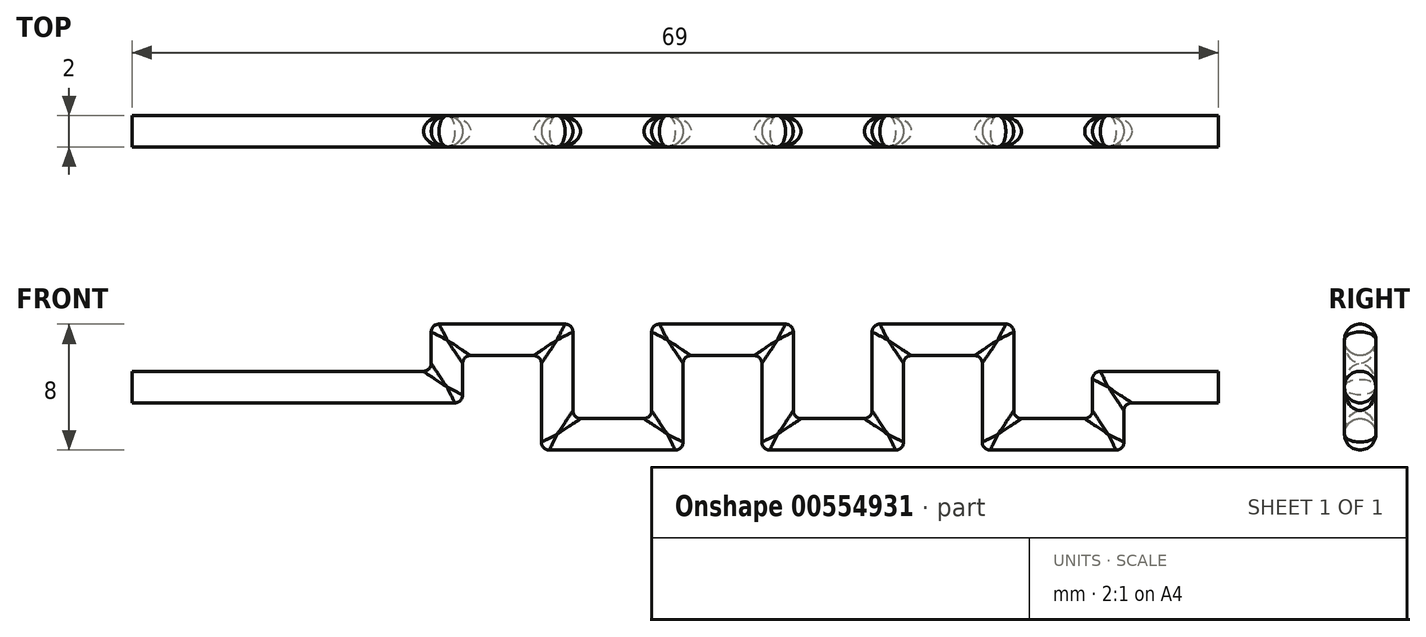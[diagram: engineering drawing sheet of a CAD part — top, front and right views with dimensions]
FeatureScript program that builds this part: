
annotation { "Feature Type Name" : "Feature", "Feature Type Description" : "" }
export const myFeature = defineFeature(function(context is Context, id is Id, definition is map)
    precondition{}
    {
        {
            var Q0;
            Q0=qCreatedBy(makeId("Front.planeOp"),FACE);
            var sketch = newSketch(context, id + "F0", { "sketchPlane" : qUnion([Q0])});
            skLineSegment(sketch, "E0", {"start": v(0, 0) * mm, "end": v(15, 0) * mm});
            skLineSegment(sketch, "E1", {"start": v(15, 0) * mm, "end": v(15, 3) * mm});
            skLineSegment(sketch, "E2", {"start": v(15, 3) * mm, "end": v(22, 3) * mm});
            skLineSegment(sketch, "E3", {"start": v(22, 3) * mm, "end": v(22, -3) * mm});
            skLineSegment(sketch, "E4", {"start": v(22, -3) * mm, "end": v(29, -3) * mm});
            skLineSegment(sketch, "E5", {"start": v(29, -3) * mm, "end": v(29, 3) * mm});
            skLineSegment(sketch, "E6", {"start": v(29, 3) * mm, "end": v(36, 3) * mm});
            skLineSegment(sketch, "E7", {"start": v(36, 3) * mm, "end": v(36, -3) * mm});
            skLineSegment(sketch, "E8", {"start": v(36, -3) * mm, "end": v(43, -3) * mm});
            skLineSegment(sketch, "E9", {"start": v(43, -3) * mm, "end": v(43, 3) * mm});
            skLineSegment(sketch, "E10", {"start": v(43, 3) * mm, "end": v(50, 3) * mm});
            skLineSegment(sketch, "E11", {"start": v(50, 3) * mm, "end": v(50, -3) * mm});
            skLineSegment(sketch, "E12", {"start": v(50, -3) * mm, "end": v(57, -3) * mm});
            skLineSegment(sketch, "E13", {"start": v(57, -3) * mm, "end": v(57, 0) * mm});
            skLineSegment(sketch, "E14.trimOffspring", {"start": v(57, 0) * mm, "end": v(64, 0) * mm});
            skSolve(sketch);
        }
        {
            var Q0;
            Q0=qCreatedBy(makeId("Right.planeOp"),FACE);
            var sketch = newSketch(context, id + "F1", { "sketchPlane" : qUnion([Q0])});
            skCircle(sketch, "E15", {"center": v(0, 0) * mm, "radius": 1 * mm});
            skSolve(sketch);
        }
        {
            var Q0;
            Q0=makeQuery(id+"F1.imprint","IMPRINT",FACE,{"disambiguationData":[TD([[makeQuery(id+"F1.imprint","IMPRINT",EDGE,{"derivedFrom":sQuery(id+"F1.wireOp",EDGE,"E15")}),1.0]])]});
            var Q1;
            Q1 = qConstructionFilter(qBodyType(qCreatedBy(id + "F0" ,EDGE), BodyType.WIRE), ConstructionObject.NO);
            sweep(context, id + "F2", {"profiles" : qUnion([Q0]), "path" : qUnion([Q1])});
        }
        {
            var Q0;
            Q0=makeQuery(id+"F2.opSweep","MID_CAP_EDGE",EDGE,{"disambiguationData":[OSD([sQuery(id+"F0.wireOp",VERTEX,"E14.trimOffspring.start"),sQuery(id+"F1.wireOp",EDGE,"E15")])],"capPos":14.0});
            var Q1;
            Q1=makeQuery(id+"F2.opSweep","MID_CAP_EDGE",EDGE,{"disambiguationData":[OSD([sQuery(id+"F0.wireOp",VERTEX,"E13.start"),sQuery(id+"F1.wireOp",EDGE,"E15")])],"capPos":13.0});
            var Q2;
            Q2=makeQuery(id+"F2.opSweep","MID_CAP_EDGE",EDGE,{"disambiguationData":[OSD([sQuery(id+"F0.wireOp",VERTEX,"E12.start"),sQuery(id+"F1.wireOp",EDGE,"E15")])],"capPos":12.0});
            var Q3;
            Q3=makeQuery(id+"F2.opSweep","MID_CAP_EDGE",EDGE,{"disambiguationData":[OSD([sQuery(id+"F0.wireOp",VERTEX,"E11.start"),sQuery(id+"F1.wireOp",EDGE,"E15")])],"capPos":11.0});
            var Q4;
            Q4=makeQuery(id+"F2.opSweep","MID_CAP_EDGE",EDGE,{"disambiguationData":[OSD([sQuery(id+"F0.wireOp",VERTEX,"E10.start"),sQuery(id+"F1.wireOp",EDGE,"E15")])],"capPos":10.0});
            var Q5;
            Q5=makeQuery(id+"F2.opSweep","MID_CAP_EDGE",EDGE,{"disambiguationData":[OSD([sQuery(id+"F0.wireOp",VERTEX,"E9.start"),sQuery(id+"F1.wireOp",EDGE,"E15")])],"capPos":9.0});
            var Q6;
            Q6=makeQuery(id+"F2.opSweep","MID_CAP_EDGE",EDGE,{"disambiguationData":[OSD([sQuery(id+"F0.wireOp",VERTEX,"E8.start"),sQuery(id+"F1.wireOp",EDGE,"E15")])],"capPos":8.0});
            var Q7;
            Q7=makeQuery(id+"F2.opSweep","MID_CAP_EDGE",EDGE,{"disambiguationData":[OSD([sQuery(id+"F0.wireOp",VERTEX,"E7.start"),sQuery(id+"F1.wireOp",EDGE,"E15")])],"capPos":7.0});
            var Q8;
            Q8=makeQuery(id+"F2.opSweep","MID_CAP_EDGE",EDGE,{"disambiguationData":[OSD([sQuery(id+"F0.wireOp",VERTEX,"E6.start"),sQuery(id+"F1.wireOp",EDGE,"E15")])],"capPos":6.0});
            var Q9;
            Q9=makeQuery(id+"F2.opSweep","MID_CAP_EDGE",EDGE,{"disambiguationData":[OSD([sQuery(id+"F0.wireOp",VERTEX,"E5.start"),sQuery(id+"F1.wireOp",EDGE,"E15")])],"capPos":5.0});
            var Q10;
            Q10=makeQuery(id+"F2.opSweep","MID_CAP_EDGE",EDGE,{"disambiguationData":[OSD([sQuery(id+"F0.wireOp",VERTEX,"E4.start"),sQuery(id+"F1.wireOp",EDGE,"E15")])],"capPos":4.0});
            var Q11;
            Q11=makeQuery(id+"F2.opSweep","MID_CAP_EDGE",EDGE,{"disambiguationData":[OSD([sQuery(id+"F0.wireOp",VERTEX,"E3.start"),sQuery(id+"F1.wireOp",EDGE,"E15")])],"capPos":3.0});
            var Q12;
            Q12=makeQuery(id+"F2.opSweep","MID_CAP_EDGE",EDGE,{"disambiguationData":[OSD([sQuery(id+"F0.wireOp",VERTEX,"E2.start"),sQuery(id+"F1.wireOp",EDGE,"E15")])],"capPos":2.0});
            var Q13;
            Q13=makeQuery(id+"F2.opSweep","MID_CAP_EDGE",EDGE,{"disambiguationData":[OSD([sQuery(id+"F0.wireOp",VERTEX,"E1.start"),sQuery(id+"F1.wireOp",EDGE,"E15")])],"capPos":1.0});
            fillet(context, id + "F3", {"entities" : qUnion([Q0, Q1, Q2, Q3, Q4, Q5, Q6, Q7, Q8, Q9, Q10, Q11, Q12, Q13]), "radius" : .5 * mm, "tangentPropagation" : true, "allowEdgeOverflow" : false});
        }
        {
            var Q0;
            Q0=makeQuery(id+"F2.opSweep","CAP_FACE",FACE,{"disambiguationData":[OSD([sQuery(id+"F0.wireOp",VERTEX,"E0.start"),sQuery(id+"F1.wireOp",EDGE,"E15")])],"isStart":true});
            var sketch = newSketch(context, id + "F4", { "sketchPlane" : qUnion([Q0])});
            skCircle(sketch, "E16", {"center": v(0, 0) * mm, "radius": 1 * mm});
            skSolve(sketch);
        }
        {
            var Q0;
            Q0 = qSketchRegion(id + "F4", true);
            extrude(context, id + "F5", {"entities" : qUnion([Q0]), "operationType" : NewBodyOperationType.ADD, "depth" : 5 * mm, "offsetDistance" : 25 * mm});
        }
    });
